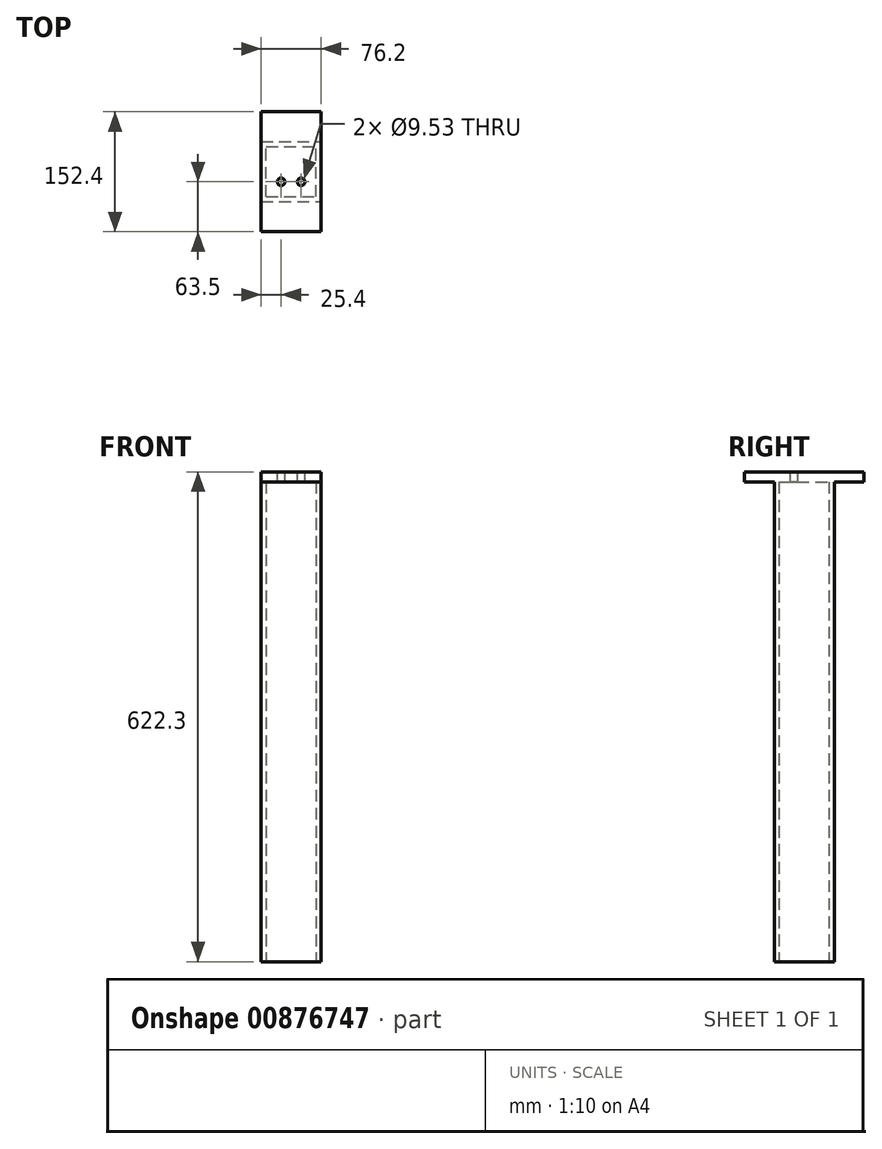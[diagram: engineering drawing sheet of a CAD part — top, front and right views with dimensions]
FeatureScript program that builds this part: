
annotation { "Feature Type Name" : "Feature", "Feature Type Description" : "" }
export const myFeature = defineFeature(function(context is Context, id is Id, definition is map)
    precondition{}
    {
        {
            var Q0;
            Q0=qCreatedBy(makeId("Top.planeOp"),FACE);
            var sketch = newSketch(context, id + "F0", { "sketchPlane" : qUnion([Q0])});
            skLineSegment(sketch, "E0.bottom", {"start": v(0, 0) * mm, "end": v(76.2, 0) * mm});
            skLineSegment(sketch, "E0.top", {"start": v(0, 76.2) * mm, "end": v(76.2, 76.2) * mm});
            skLineSegment(sketch, "E0.left", {"start": v(0, 0) * mm, "end": v(0, 76.2) * mm});
            skLineSegment(sketch, "E0.right", {"start": v(76.2, 0) * mm, "end": v(76.2, 76.2) * mm});
            skLineSegment(sketch, "E1.bottom", {"start": v(6.35, 6.35) * mm, "end": v(69.85, 6.35) * mm});
            skLineSegment(sketch, "E1.top", {"start": v(6.35, 69.85) * mm, "end": v(69.85, 69.85) * mm});
            skLineSegment(sketch, "E1.left", {"start": v(6.35, 6.35) * mm, "end": v(6.35, 69.85) * mm});
            skLineSegment(sketch, "E1.right", {"start": v(69.85, 6.35) * mm, "end": v(69.85, 69.85) * mm});
            skSolve(sketch);
        }
        {
            var Q0;
            Q0 = qSketchRegion(id + "F0", true);
            extrude(context, id + "F1", {"entities" : qUnion([Q0]), "depth" : 609.6 * mm, "offsetDistance" : 25.4 * mm});
        }
        {
            var Q0;
            Q0=makeQuery(id+"F1.opExtrude","CAP_FACE",FACE,{"disambiguationData":[OSD([sQuery(id+"F0.wireOp",EDGE,"E0.bottom"),sQuery(id+"F0.wireOp",EDGE,"E0.top"),sQuery(id+"F0.wireOp",EDGE,"E0.left"),sQuery(id+"F0.wireOp",EDGE,"E0.right"),sQuery(id+"F0.wireOp",EDGE,"E1.bottom"),sQuery(id+"F0.wireOp",EDGE,"E1.top"),sQuery(id+"F0.wireOp",EDGE,"E1.left"),sQuery(id+"F0.wireOp",EDGE,"E1.right")])],"isStart":false});
            var sketch = newSketch(context, id + "F2", { "sketchPlane" : qUnion([Q0])});
            skLineSegment(sketch, "E2.bottom", {"start": v(0, 114.3) * mm, "end": v(76.2, 114.3) * mm});
            skLineSegment(sketch, "E2.top", {"start": v(0, -38.1) * mm, "end": v(76.2, -38.1) * mm});
            skLineSegment(sketch, "E2.left", {"start": v(0, 114.3) * mm, "end": v(0, -38.1) * mm});
            skLineSegment(sketch, "E2.right", {"start": v(76.2, 114.3) * mm, "end": v(76.2, -38.1) * mm});
            skSolve(sketch);
        }
        {
            var Q0;
            Q0 = qSketchRegion(id + "F2", true);
            extrude(context, id + "F3", {"entities" : qUnion([Q0]), "operationType" : NewBodyOperationType.ADD, "depth" : 12.7 * mm, "offsetDistance" : 25.4 * mm});
        }
        {
            var Q0;
            Q0=makeQuery(id+"F3.opExtrude","CAP_FACE",FACE,{"disambiguationData":[OSD([sQuery(id+"F2.wireOp",EDGE,"E2.bottom"),sQuery(id+"F2.wireOp",EDGE,"E2.top"),sQuery(id+"F2.wireOp",EDGE,"E2.left"),sQuery(id+"F2.wireOp",EDGE,"E2.right")])],"isStart":false});
            var sketch = newSketch(context, id + "F4", { "sketchPlane" : qUnion([Q0])});
            skCircle(sketch, "E3", {"center": v(50.8, 25.4) * mm, "radius": 4.76 * mm});
            skCircle(sketch, "E4", {"center": v(25.4, 25.4) * mm, "radius": 4.76 * mm});
            skSolve(sketch);
        }
        {
            var Q0;
            Q0 = qSketchRegion(id + "F4", true);
            extrude(context, id + "F5", {"entities" : qUnion([Q0]), "operationType" : NewBodyOperationType.REMOVE, "oppositeDirection" : true, "depth" : 25.4 * mm, "offsetDistance" : 25.4 * mm});
        }
    });
